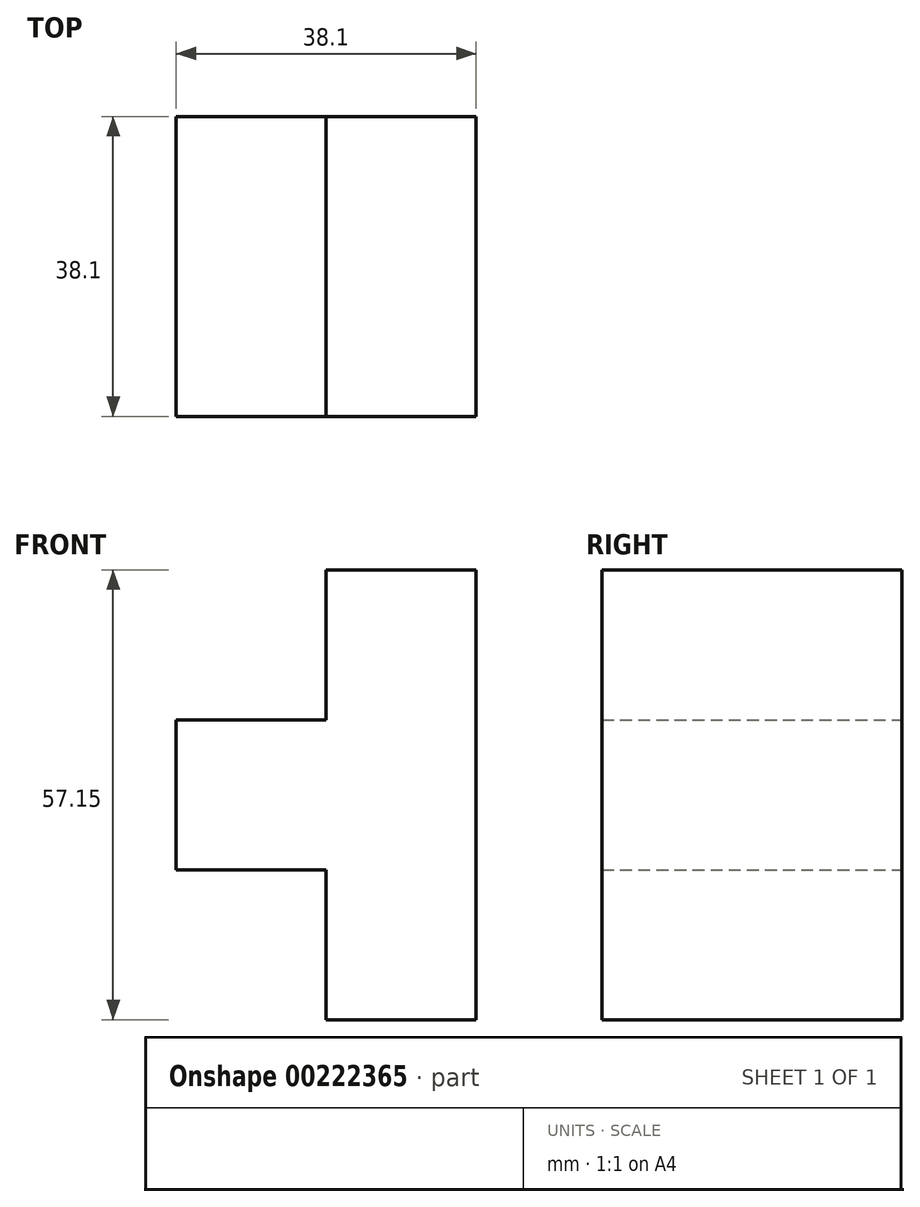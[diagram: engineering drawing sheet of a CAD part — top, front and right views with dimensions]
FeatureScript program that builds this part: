
annotation { "Feature Type Name" : "Feature", "Feature Type Description" : "" }
export const myFeature = defineFeature(function(context is Context, id is Id, definition is map)
    precondition{}
    {
        {
            var Q0;
            Q0=qCreatedBy(makeId("Front.planeOp"),FACE);
            var sketch = newSketch(context, id + "F0", { "sketchPlane" : qUnion([Q0])});
            skLineSegment(sketch, "E0.bottom", {"start": v(-37.77, 10.76) * mm, "end": v(-56.82, 10.76) * mm});
            skLineSegment(sketch, "E0.top", {"start": v(-37.77, 67.9) * mm, "end": v(-56.82, 67.9) * mm});
            skLineSegment(sketch, "E0.left", {"start": v(-37.77, 10.76) * mm, "end": v(-37.77, 67.9) * mm});
            skLineSegment(sketch, "E0.right", {"start": v(-56.82, 10.76) * mm, "end": v(-56.82, 67.9) * mm});
            skPoint(sketch, "E0.middle", {"position": v(-47.3, 39.33) * mm});
            skLineSegment(sketch, "E1.bottom", {"start": v(-56.82, 29.8) * mm, "end": v(-75.87, 29.8) * mm});
            skLineSegment(sketch, "E1.top", {"start": v(-56.82, 48.86) * mm, "end": v(-75.87, 48.86) * mm});
            skLineSegment(sketch, "E1.left", {"start": v(-56.82, 29.8) * mm, "end": v(-56.82, 48.86) * mm});
            skLineSegment(sketch, "E1.right", {"start": v(-75.87, 29.8) * mm, "end": v(-75.87, 48.86) * mm});
            skPoint(sketch, "E1.middle", {"position": v(-66.35, 39.33) * mm});
            skPoint(sketch, "E2.endSnap0", {"position": v(-56.82, 39.33) * mm});
            skSolve(sketch);
        }
        {
            var Q0;
            Q0=qSketchRegion(id+"F0",true);
            extrude(context, id + "F1", {"entities" : qUnion([Q0]), "depth" : 25.4 * mm});
        }
        {
            var Q0;
            Q0=qSketchRegion(id+"F0",true);
            extrude(context, id + "F2", {"entities" : qUnion([Q0]), "operationType" : NewBodyOperationType.ADD, "endBound" : BoundingType.SYMMETRIC, "depth" : 25.4 * mm});
        }
        {
            var Q0;
            Q0=qSketchRegion(id+"F0",true);
            extrude(context, id + "F3", {"entities" : qUnion([Q0]), "operationType" : NewBodyOperationType.ADD, "endBound" : BoundingType.SYMMETRIC, "depth" : 25.4 * mm});
        }
    });
